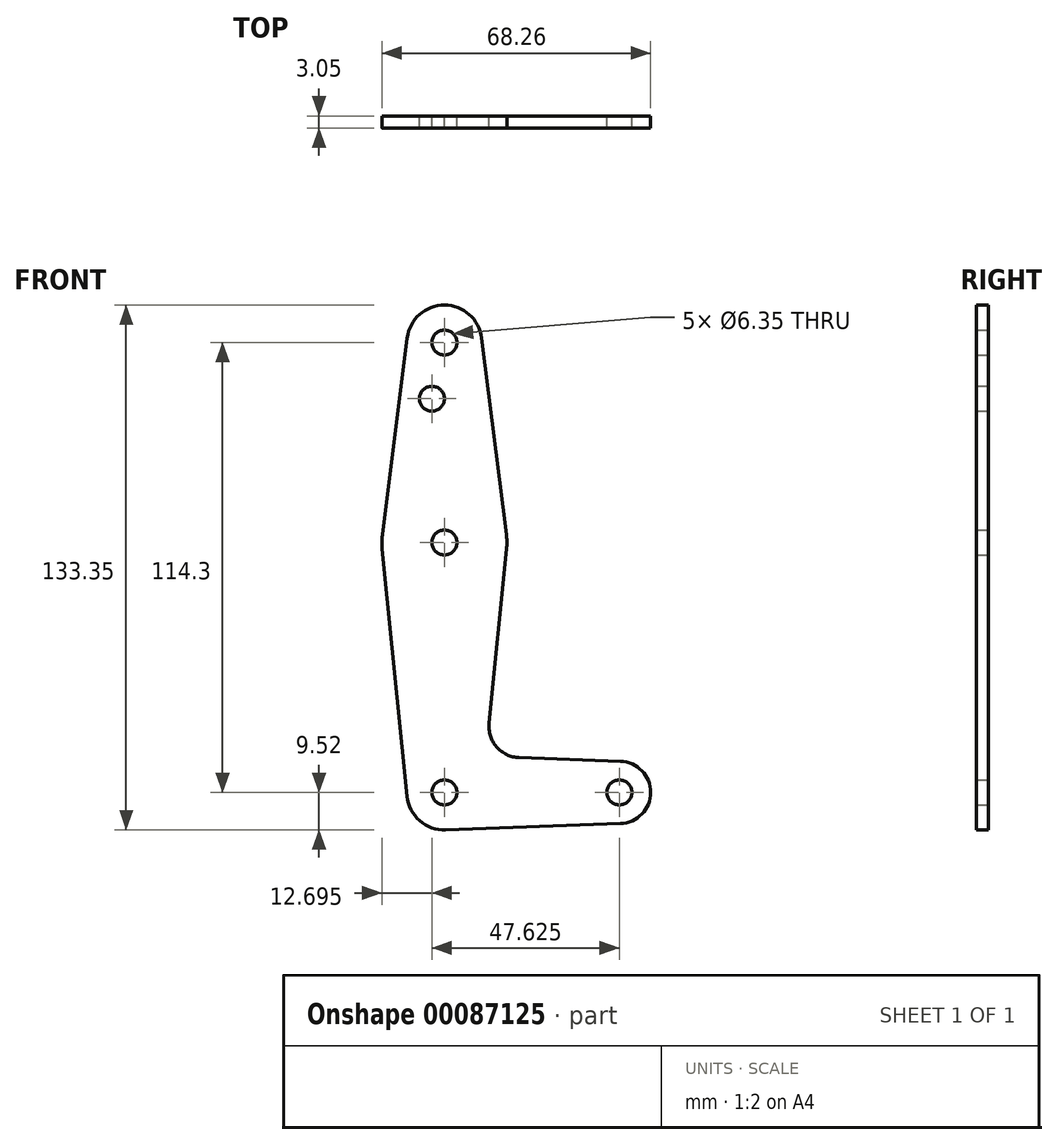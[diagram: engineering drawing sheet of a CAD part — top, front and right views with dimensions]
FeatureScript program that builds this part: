
annotation { "Feature Type Name" : "Feature", "Feature Type Description" : "" }
export const myFeature = defineFeature(function(context is Context, id is Id, definition is map)
    precondition{}
    {
        {
            var Q0;
            Q0=qCreatedBy(makeId("Front.planeOp"),FACE);
            var sketch = newSketch(context, id + "F0", { "sketchPlane" : qUnion([Q0])});
            skLineSegment(sketch, "E0", {"start": v(0, 0) * mm, "end": v(44.45, 0) * mm, "construction": true});
            skCircle(sketch, "E1", {"center": v(0, 63.5) * mm, "radius": 15.88 * mm});
            skCircle(sketch, "E2", {"center": v(0, 114.3) * mm, "radius": 9.53 * mm});
            skCircle(sketch, "E3", {"center": v(0, 0) * mm, "radius": 9.53 * mm});
            skCircle(sketch, "E4", {"center": v(44.45, 0) * mm, "radius": 7.94 * mm});
            skLineSegment(sketch, "E5", {"start": v(0, 114.3) * mm, "end": v(0, 0) * mm, "construction": true});
            skLineSegment(sketch, "E6", {"start": v(-9.45, 115.5) * mm, "end": v(-15.75, 65.48) * mm});
            skLineSegment(sketch, "E7", {"start": v(9.45, 115.5) * mm, "end": v(15.75, 65.48) * mm});
            skLineSegment(sketch, "E8", {"start": v(-15.8, 61.91) * mm, "end": v(-9.48, -0.95) * mm});
            skLineSegment(sketch, "E9", {"start": v(15.8, 61.91) * mm, "end": v(11.34, 17.6) * mm});
            skLineSegment(sketch, "E10", {"start": v(18.97, 8.85) * mm, "end": v(44.73, 7.93) * mm});
            skPoint(sketch, "E11.startSnap0", {"position": v(0, 57.15) * mm});
            skLineSegment(sketch, "E12", {"start": v(0.34, -9.52) * mm, "end": v(44.73, -7.93) * mm});
            skCircle(sketch, "E13", {"center": v(0, 114.3) * mm, "radius": 3.18 * mm});
            skCircle(sketch, "E14", {"center": v(-3.17, 100.03) * mm, "radius": 3.18 * mm});
            skCircle(sketch, "E15", {"center": v(0, 63.5) * mm, "radius": 3.18 * mm});
            skCircle(sketch, "E16", {"center": v(0, 0) * mm, "radius": 3.18 * mm});
            skCircle(sketch, "E17", {"center": v(44.45, 0) * mm, "radius": 3.18 * mm});
            skArc(sketch, "E18.filletArc", {"start": v(11.34, 17.6) * mm, "mid": v(13.26, 11.57) * mm, "end": v(18.97, 8.85) * mm});
            skSolve(sketch);
        }
        {
            var Q0;
            Q0=makeQuery(id+"F0.imprint","IMPRINT",FACE,{"disambiguationData":[TD([[makeQuery(id+"F0.imprint","IMPRINT",EDGE,{"derivedFrom":sQuery(id+"F0.wireOp",EDGE,"E13")}),-1.0]])]});
            var Q1;
            {var subQ1=sQuery(id+"F0.wireOp",EDGE,"E6");Q1=makeQuery(id+"F0.imprint","IMPRINT",FACE,{"disambiguationData":[TD([[makeQuery(id+"F0.imprint","IMPRINT",EDGE,{"derivedFrom":subQ1}),1.0]])]});}
            var Q2;
            Q2=makeQuery(id+"F0.imprint","IMPRINT",FACE,{"disambiguationData":[TD([[makeQuery(id+"F0.imprint","IMPRINT",EDGE,{"derivedFrom":sQuery(id+"F0.wireOp",EDGE,"E15")}),-1.0]])]});
            var Q3;
            {var subQ0=sQuery(id+"F0.wireOp",EDGE,"E8");Q3=makeQuery(id+"F0.imprint","IMPRINT",FACE,{"disambiguationData":[TD([[makeQuery(id+"F0.imprint","IMPRINT",EDGE,{"derivedFrom":subQ0}),1.0]])]});}
            var Q4;
            Q4=makeQuery(id+"F0.imprint","IMPRINT",FACE,{"disambiguationData":[TD([[makeQuery(id+"F0.imprint","IMPRINT",EDGE,{"derivedFrom":sQuery(id+"F0.wireOp",EDGE,"E16")}),-1.0]])]});
            var Q5;
            Q5=makeQuery(id+"F0.imprint","IMPRINT",FACE,{"disambiguationData":[TD([[makeQuery(id+"F0.imprint","IMPRINT",EDGE,{"derivedFrom":sQuery(id+"F0.wireOp",EDGE,"E17")}),-1.0]])]});
            extrude(context, id + "F1", {"entities" : qUnion([Q0, Q1, Q2, Q3, Q4, Q5]), "depth" : 3.05 * mm});
        }
    });
